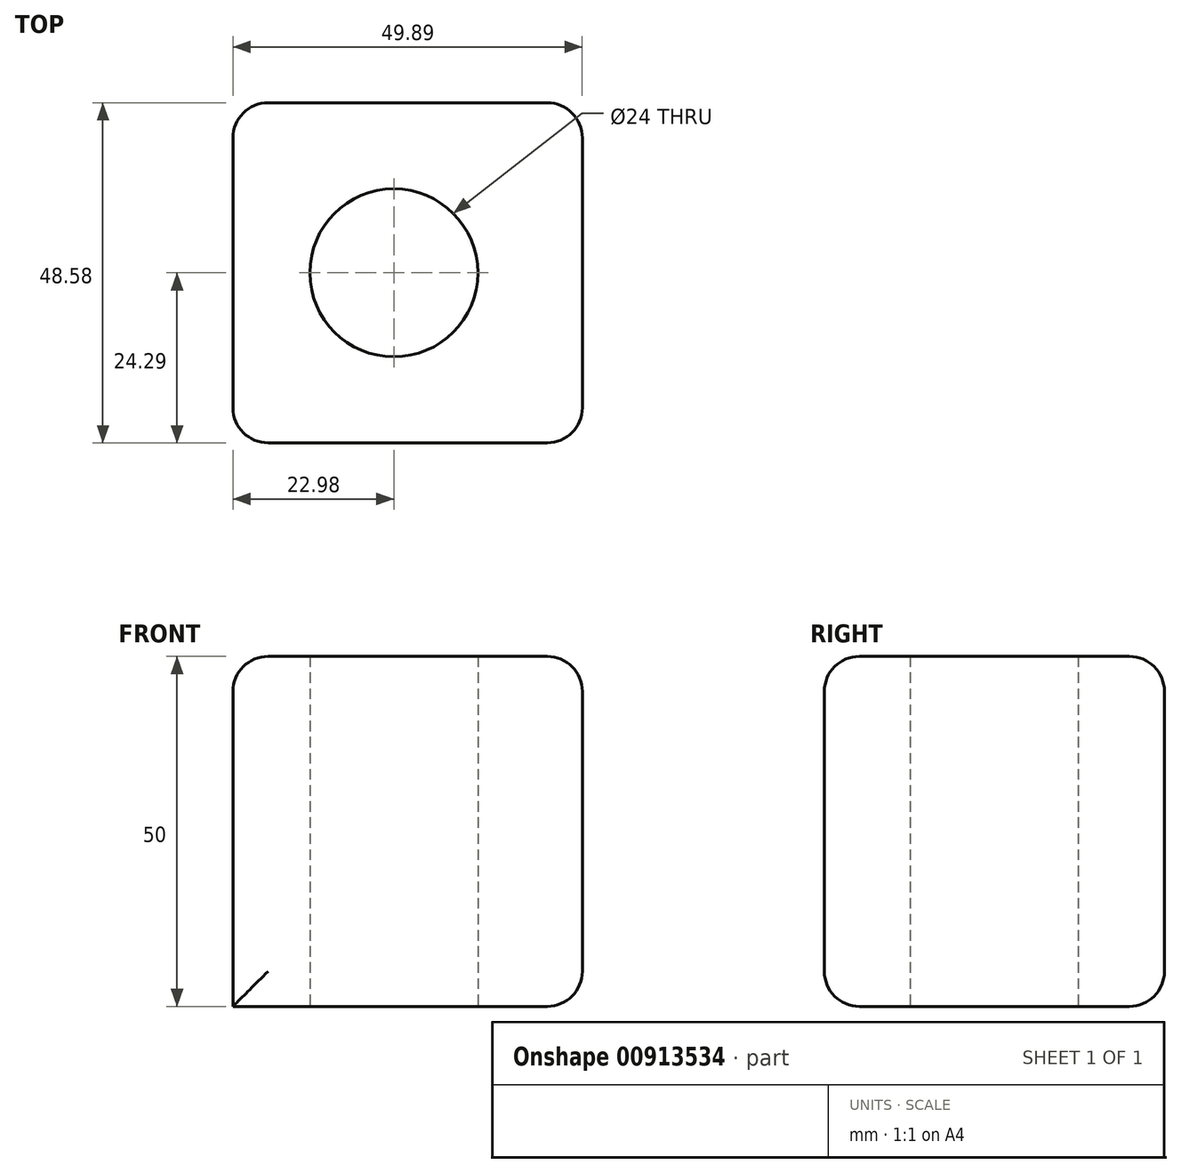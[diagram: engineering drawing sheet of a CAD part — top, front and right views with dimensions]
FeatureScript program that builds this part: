
annotation { "Feature Type Name" : "Feature", "Feature Type Description" : "" }
export const myFeature = defineFeature(function(context is Context, id is Id, definition is map)
    precondition{}
    {
        {
            var Q0;
            Q0=qCreatedBy(makeId("Top.planeOp"),FACE);
            var sketch = newSketch(context, id + "F0", { "sketchPlane" : qUnion([Q0])});
            skLineSegment(sketch, "E0.bottom", {"start": v(26.91, 24.29) * mm, "end": v(-22.98, 24.29) * mm});
            skLineSegment(sketch, "E0.top", {"start": v(26.91, -24.29) * mm, "end": v(-22.98, -24.29) * mm});
            skLineSegment(sketch, "E0.left", {"start": v(26.91, 24.29) * mm, "end": v(26.91, -24.29) * mm});
            skLineSegment(sketch, "E0.right", {"start": v(-22.98, 24.29) * mm, "end": v(-22.98, -24.29) * mm});
            skPoint(sketch, "E0.middle", {"position": v(1.97, 0) * mm});
            skCircle(sketch, "E1", {"center": v(0, 0) * mm, "radius": 12 * mm});
            skSolve(sketch);
        }
        {
            var Q0;
            Q0 = qSketchRegion(id + "F0", true);
            extrude(context, id + "F1", {"entities" : qUnion([Q0]), "endBound" : BoundingType.SYMMETRIC, "depth" : 50 * mm, "offsetDistance" : 25 * mm});
        }
        {
            var Q0;
            Q0=makeQuery(id+"F1.opExtrude","SWEPT_EDGE",EDGE,{"disambiguationData":[OSD([sQuery(id+"F0.wireOp",EDGE,"E0.bottom"),sQuery(id+"F0.wireOp",EDGE,"E0.right")])]});
            var Q1;
            Q1=makeQuery(id+"F1.opExtrude","CAP_EDGE",EDGE,{"disambiguationData":[OSD([sQuery(id+"F0.wireOp",EDGE,"E0.bottom")])],"isStart":false});
            var Q2;
            Q2=makeQuery(id+"F1.opExtrude","CAP_EDGE",EDGE,{"disambiguationData":[OSD([sQuery(id+"F0.wireOp",EDGE,"E0.right")])],"isStart":false});
            var Q3;
            Q3=makeQuery(id+"F1.opExtrude","SWEPT_EDGE",EDGE,{"disambiguationData":[OSD([sQuery(id+"F0.wireOp",EDGE,"E0.top"),sQuery(id+"F0.wireOp",EDGE,"E0.right")])]});
            var Q4;
            Q4=makeQuery(id+"F1.opExtrude","CAP_EDGE",EDGE,{"disambiguationData":[OSD([sQuery(id+"F0.wireOp",EDGE,"E0.left")])],"isStart":false});
            var Q5;
            Q5=makeQuery(id+"F1.opExtrude","CAP_EDGE",EDGE,{"disambiguationData":[OSD([sQuery(id+"F0.wireOp",EDGE,"E0.top")])],"isStart":false});
            var Q6;
            Q6=makeQuery(id+"F1.opExtrude","SWEPT_EDGE",EDGE,{"disambiguationData":[OSD([sQuery(id+"F0.wireOp",EDGE,"E0.bottom"),sQuery(id+"F0.wireOp",EDGE,"E0.left")])]});
            var Q7;
            Q7=makeQuery(id+"F1.opExtrude","SWEPT_EDGE",EDGE,{"disambiguationData":[OSD([sQuery(id+"F0.wireOp",EDGE,"E0.top"),sQuery(id+"F0.wireOp",EDGE,"E0.left")])]});
            var Q8;
            Q8=makeQuery(id+"F1.opExtrude","CAP_EDGE",EDGE,{"disambiguationData":[OSD([sQuery(id+"F0.wireOp",EDGE,"E0.left")])],"isStart":true});
            var Q9;
            Q9=makeQuery(id+"F1.opExtrude","CAP_EDGE",EDGE,{"disambiguationData":[OSD([sQuery(id+"F0.wireOp",EDGE,"E0.bottom")])],"isStart":true});
            var Q10;
            Q10=makeQuery(id+"F1.opExtrude","CAP_EDGE",EDGE,{"disambiguationData":[OSD([sQuery(id+"F0.wireOp",EDGE,"E0.top")])],"isStart":true});
            fillet(context, id + "F2", {"entities" : qUnion([Q0, Q1, Q2, Q3, Q4, Q5, Q6, Q7, Q8, Q9, Q10]), "radius" : 5 * mm, "tangentPropagation" : true, "allowEdgeOverflow" : false});
        }
    });
